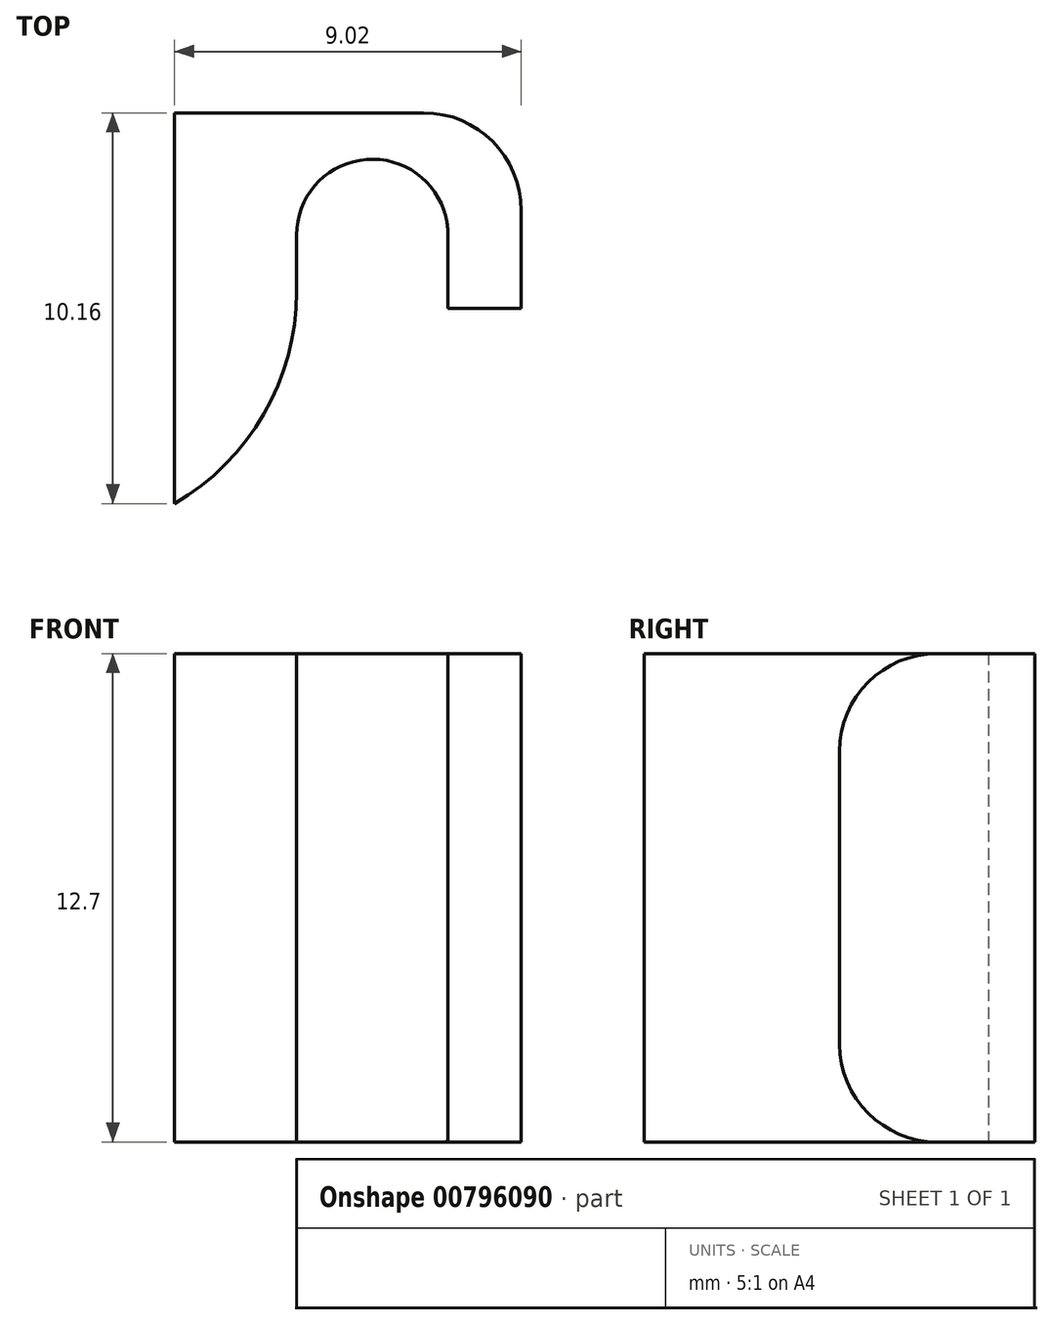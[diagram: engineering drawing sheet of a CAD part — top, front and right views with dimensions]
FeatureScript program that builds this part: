
annotation { "Feature Type Name" : "Feature", "Feature Type Description" : "" }
export const myFeature = defineFeature(function(context is Context, id is Id, definition is map)
    precondition{}
    {
        {
            var Q0;
            Q0=qCreatedBy(makeId("Top.planeOp"),FACE);
            var sketch = newSketch(context, id + "F0", { "sketchPlane" : qUnion([Q0])});
            skLineSegment(sketch, "E0.top", {"start": v(0, -5.08) * mm, "end": v(3.17, -5.08) * mm});
            skLineSegment(sketch, "E0.left", {"start": v(0, 5.08) * mm, "end": v(0, -5.08) * mm});
            skLineSegment(sketch, "E1", {"start": v(0, 5.08) * mm, "end": v(9.02, 5.08) * mm});
            skLineSegment(sketch, "E2", {"start": v(9.02, 5.08) * mm, "end": v(9.02, 0) * mm});
            skLineSegment(sketch, "E3", {"start": v(9.02, 0) * mm, "end": v(7.11, 0) * mm});
            skLineSegment(sketch, "E4", {"start": v(7.11, 0) * mm, "end": v(7.11, 1.9) * mm});
            skArc(sketch, "E5", {"start": v(7.11, 1.9) * mm, "mid": v(5.14, 3.87) * mm, "end": v(3.18, 1.9) * mm});
            skLineSegment(sketch, "E6", {"start": v(3.18, 1.9) * mm, "end": v(3.17, -5.08) * mm});
            skSolve(sketch);
        }
        {
            var Q0;
            Q0 = qSketchRegion(id + "F0", true);
            extrude(context, id + "F1", {"entities" : qUnion([Q0]), "depth" : 12.7 * mm, "offsetDistance" : 25.4 * mm});
        }
        {
            var Q0;
            Q0=makeQuery(id+"F1.opExtrude","SWEPT_EDGE",EDGE,{"disambiguationData":[OSD([sQuery(id+"F0.wireOp",EDGE,"E1"),sQuery(id+"F0.wireOp",EDGE,"E2")])]});
            fillet(context, id + "F2", {"entities" : qUnion([Q0]), "radius" : 2.54 * mm, "tangentPropagation" : true, "allowEdgeOverflow" : false});
        }
        {
            var Q0;
            Q0=makeQuery(id+"F1.opExtrude","SWEPT_EDGE",EDGE,{"disambiguationData":[OSD([sQuery(id+"F0.wireOp",EDGE,"E0.top"),sQuery(id+"F0.wireOp",EDGE,"E6")])]});
            fillet(context, id + "F3", {"entities" : qUnion([Q0]), "radius" : 6.35 * mm, "tangentPropagation" : true, "allowEdgeOverflow" : false});
        }
        {
            var Q0;
            Q0=makeQuery(id+"F1.opExtrude","CAP_EDGE",EDGE,{"disambiguationData":[OSD([sQuery(id+"F0.wireOp",EDGE,"E3")])],"isStart":false});
            var Q1;
            Q1=makeQuery(id+"F1.opExtrude","CAP_EDGE",EDGE,{"disambiguationData":[OSD([sQuery(id+"F0.wireOp",EDGE,"E3")])],"isStart":true});
            fillet(context, id + "F4", {"entities" : qUnion([Q0, Q1]), "radius" : 2.54 * mm, "tangentPropagation" : true, "allowEdgeOverflow" : false});
        }
    });
